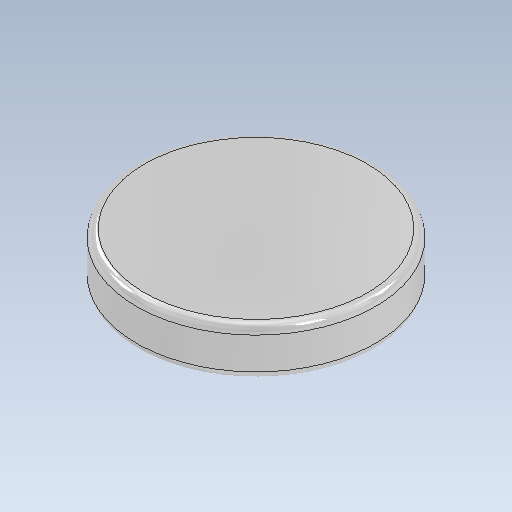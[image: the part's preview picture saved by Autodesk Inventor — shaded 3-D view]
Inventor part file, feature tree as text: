
AUTODESK INVENTOR PART (.ipt)
format: ipt  version: 2020 (Build 240168000, 168)  size: 119,808 bytes
history: native  units: mm
features: extrude x1, fillet x1, sketch x1
ambient origin geometry x8: Origin, YZ Plane, XZ Plane, XY Plane, X Axis, Y Axis, Z Axis, Center Point
bodies: Volumenkörper1 (feature_tree)
feature tree (3):
  extrude  "Extrusion1"  Depth=3.0mm TaperAngle=0.0deg
  fillet  "Rundung1"  Radius=0.5mm
  sketch  "Skizze1"  dims[d0=15.0mm d1=3.0mm d2=0.0mm d3=0.5mm]
